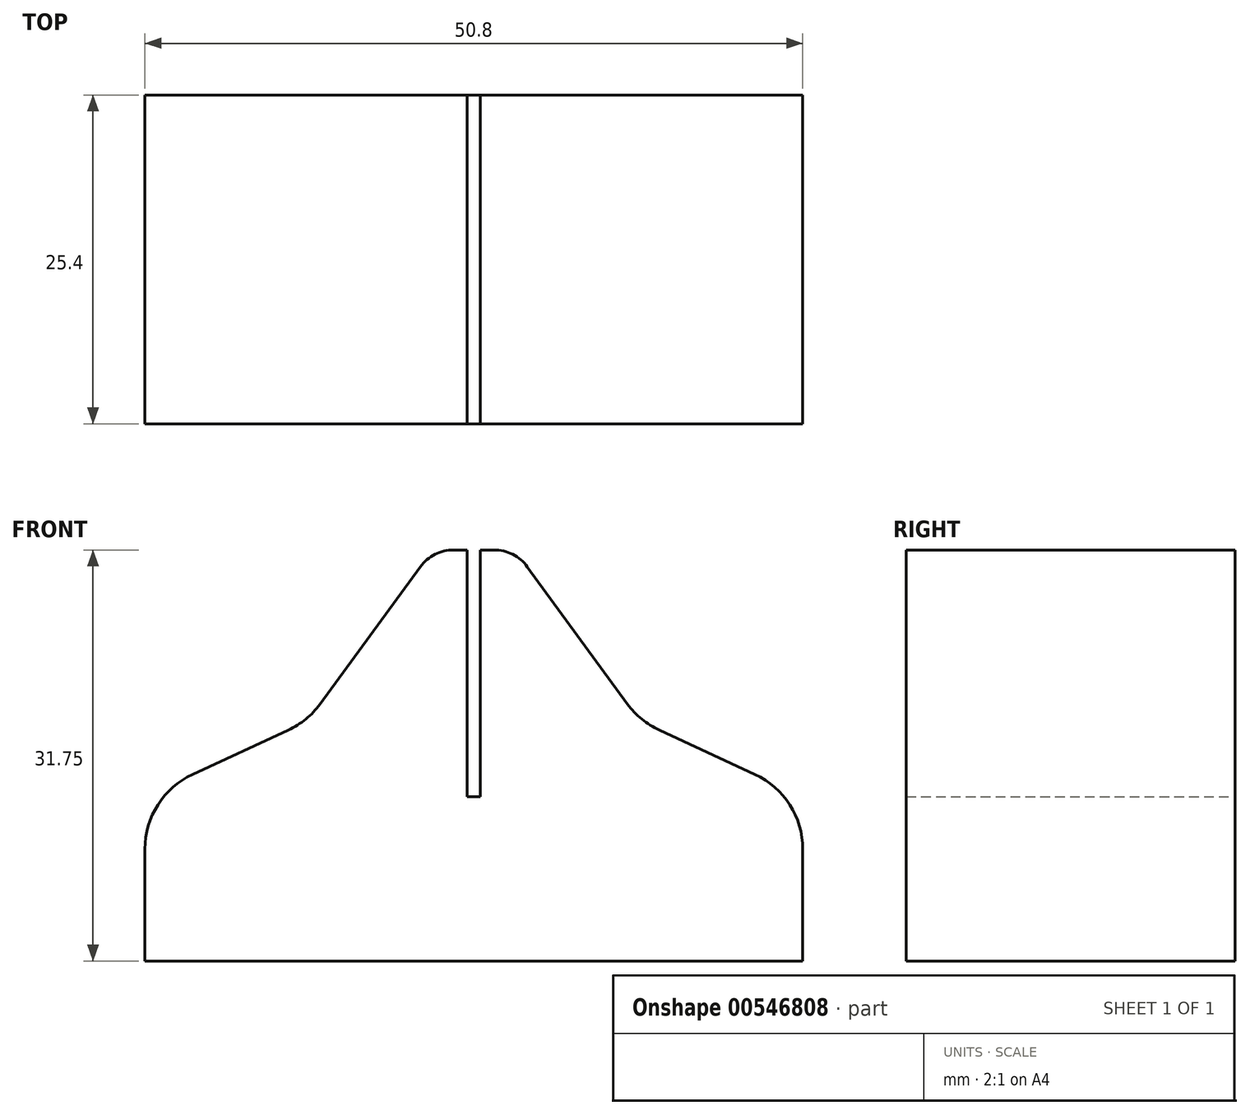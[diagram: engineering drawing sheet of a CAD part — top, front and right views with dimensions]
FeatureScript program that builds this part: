
annotation { "Feature Type Name" : "Feature", "Feature Type Description" : "" }
export const myFeature = defineFeature(function(context is Context, id is Id, definition is map)
    precondition{}
    {
        {
            var Q0;
            Q0=qCreatedBy(makeId("Front.planeOp"),FACE);
            var sketch = newSketch(context, id + "F0", { "sketchPlane" : qUnion([Q0])});
            skLineSegment(sketch, "E0", {"start": v(25.4, 0) * mm, "end": v(25.4, 12.7) * mm});
            skLineSegment(sketch, "E1", {"start": v(25.4, 12.7) * mm, "end": v(12.84, 18.52) * mm});
            skLineSegment(sketch, "E2", {"start": v(12.84, 18.52) * mm, "end": v(3.17, 31.75) * mm});
            skLineSegment(sketch, "E3", {"start": v(3.18, 31.75) * mm, "end": v(0.5, 31.75) * mm});
            skLineSegment(sketch, "E4", {"start": v(0.5, 31.75) * mm, "end": v(0.5, 12.7) * mm});
            skLineSegment(sketch, "E5.MirrorCS", {"start": v(-0.5, 31.75) * mm, "end": v(-0.5, 12.7) * mm});
            skLineSegment(sketch, "E6.MirrorCS", {"start": v(-3.18, 31.75) * mm, "end": v(-0.5, 31.75) * mm});
            skLineSegment(sketch, "E7.MirrorCS", {"start": v(-12.84, 18.52) * mm, "end": v(-3.17, 31.75) * mm});
            skLineSegment(sketch, "E8.MirrorCS", {"start": v(-25.4, 12.7) * mm, "end": v(-12.84, 18.52) * mm});
            skLineSegment(sketch, "E9.MirrorCS", {"start": v(-25.4, 0) * mm, "end": v(-25.4, 12.7) * mm});
            skLineSegment(sketch, "E10", {"start": v(-0.5, 12.7) * mm, "end": v(0.5, 12.7) * mm});
            skLineSegment(sketch, "E11", {"start": v(-25.4, 0) * mm, "end": v(25.4, 0) * mm});
            skSolve(sketch);
        }
        {
            var Q0;
            Q0=makeQuery(id+"F0.imprint","IMPRINT",FACE,{"disambiguationData":[TD([[makeQuery(id+"F0.imprint","IMPRINT",EDGE,{"derivedFrom":sQuery(id+"F0.wireOp",EDGE,"E0")}),1.0]])]});
            extrude(context, id + "F1", {"entities" : qUnion([Q0]), "endBound" : BoundingType.SYMMETRIC, "depth" : 25.4 * mm, "offsetDistance" : 25.4 * mm});
        }
        {
            var Q0;
            Q0=makeQuery(id+"F1.opExtrude","SWEPT_EDGE",EDGE,{"disambiguationData":[OSD([sQuery(id+"F0.wireOp",EDGE,"E0"),sQuery(id+"F0.wireOp",EDGE,"E1")])]});
            var Q1;
            Q1=makeQuery(id+"F1.opExtrude","SWEPT_EDGE",EDGE,{"disambiguationData":[OSD([sQuery(id+"F0.wireOp",EDGE,"E1"),sQuery(id+"F0.wireOp",EDGE,"E2")])]});
            var Q2;
            Q2=makeQuery(id+"F1.opExtrude","SWEPT_EDGE",EDGE,{"disambiguationData":[OSD([sQuery(id+"F0.wireOp",EDGE,"E7.MirrorCS"),sQuery(id+"F0.wireOp",EDGE,"E8.MirrorCS")])]});
            var Q3;
            Q3=makeQuery(id+"F1.opExtrude","SWEPT_EDGE",EDGE,{"disambiguationData":[OSD([sQuery(id+"F0.wireOp",EDGE,"E8.MirrorCS"),sQuery(id+"F0.wireOp",EDGE,"E9.MirrorCS")])]});
            fillet(context, id + "F2", {"entities" : qUnion([Q0, Q1, Q2, Q3]), "radius" : 6.35 * mm, "tangentPropagation" : true, "allowEdgeOverflow" : false});
        }
        {
            var Q0;
            Q0=makeQuery(id+"F1.opExtrude","SWEPT_EDGE",EDGE,{"disambiguationData":[OSD([sQuery(id+"F0.wireOp",EDGE,"E2"),sQuery(id+"F0.wireOp",EDGE,"E3")])]});
            var Q1;
            Q1=makeQuery(id+"F1.opExtrude","SWEPT_EDGE",EDGE,{"disambiguationData":[OSD([sQuery(id+"F0.wireOp",EDGE,"E6.MirrorCS"),sQuery(id+"F0.wireOp",EDGE,"E7.MirrorCS")])]});
            fillet(context, id + "F3", {"entities" : qUnion([Q0, Q1]), "radius" : 3.17 * mm, "tangentPropagation" : true, "allowEdgeOverflow" : false});
        }
    });
